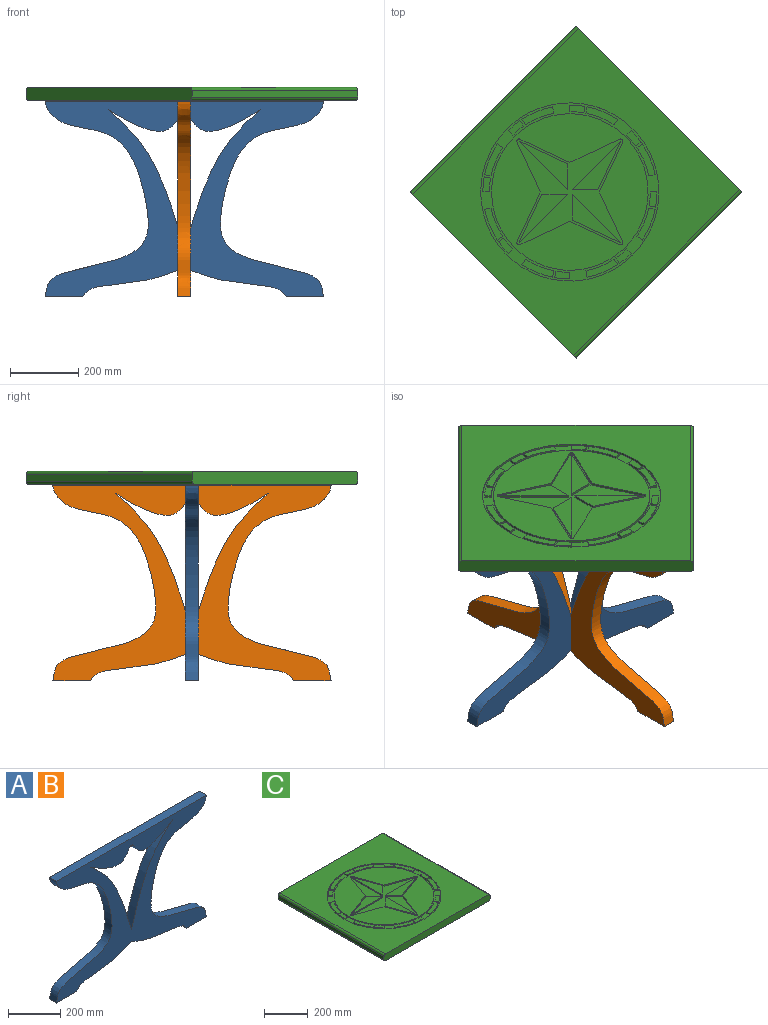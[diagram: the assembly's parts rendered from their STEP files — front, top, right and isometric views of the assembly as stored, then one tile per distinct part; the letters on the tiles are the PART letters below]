
ASSEMBLY  parts=3 mates=1
PART A: 13 faces, bbox 812.8x38.1x571.5 mm
  f0: extruded ~296.91x85.34mm, area 12012.6mm2, adj f1,f10,f11,f12
  f1: plane 109.49x38.1mm, normal (0,0,-1), area 4171.7mm2, adj f0,f2,f11,f12
  f2: extruded ~571.5x300.4mm, area 35398.5mm2, adj f1,f3,f11,f12
  f3: plane 812.8x38.1mm, normal (0,0,1), area 30967.7mm2, adj f2,f4,f11,f12
  f4: extruded ~571.5x300.4mm, area 35398.5mm2, adj f3,f5,f11,f12
  f5: plane 109.49x38.1mm, normal (0,0,-1), area 4171.7mm2, adj f4,f10,f11,f12
  f6: extruded ~58.88x53.54mm, area 3171mm2, adj f7,f9,f11,f12
  f7: extruded ~405.73x222.25mm, area 24861.6mm2, adj f6,f8,f11,f12
  f8: extruded ~405.73x222.25mm, area 24861.6mm2, adj f7,f9,f11,f12
  f9: extruded ~58.88x53.54mm, area 3171mm2, adj f6,f8,f11,f12
  f10: extruded ~296.91x85.34mm, area 12012.6mm2, adj f0,f5,f11,f12
  f11: plane 812.8x571.5mm, normal (0,-1,0), area 168324.2mm2, adj f0,f1,f2,f3,f4,f5,f6,f7
  f12: plane 812.8x571.5mm, normal (0,1,0), area 168324.2mm2, adj f0,f1,f2,f3,f4,f5,f6,f7
PART B: same geometry as A
PART C: 123 faces, bbox 685.8x685.8x38.1 mm
  f0: plane 457.2x457.2mm, normal (0,0,1), area 108640mm2, adj f76,f96,f97,f98,f99,f100,f101,f102
  f1: plane 685.8x666.75mm, normal (0,0,1), area 244313.3mm2, adj f3,f5,f9,f10,f59
  f2: plane 685.8x19.05mm, normal (-1,0,0), area 13064.5mm2, adj f3,f5,f8,f10
  f3: plane 685.8x38.1mm, normal (0,-1,0), area 26051.1mm2, adj f1,f2,f4,f6,f7,f8,f9,f10
  f4: plane 685.8x19.05mm, normal (1,0,0), area 13064.5mm2, adj f3,f5,f7,f9
  f5: plane 685.8x38.1mm, normal (0,1,0), area 26051.1mm2, adj f1,f2,f4,f6,f7,f8,f9,f10
  f6: plane 685.8x666.75mm, normal (0,0,-1), area 457257.1mm2, adj f3,f5,f7,f8
  f7: cylinder r=9.53mm len=685.8mm, axis (0,1,0), area 10260.8mm2, adj f3,f4,f5,f6
  f8: cylinder r=9.53mm len=685.8mm, axis (0,-1,0), area 10260.8mm2, adj f2,f3,f5,f6
  f9: cylinder r=9.53mm len=685.8mm, axis (0,-1,0), area 10260.8mm2, adj f1,f3,f4,f5
  f10: cylinder r=9.53mm len=685.8mm, axis (0,1,0), area 10260.8mm2, adj f1,f2,f3,f5
  f11: cylinder r=254mm len=90.1mm, axis (0,0,1), area 623.1mm2, adj f12,f60,f77,f93
  f12: plane 18.77x6.35mm, normal (0.17,-0.98,0), area 121mm2, adj f11,f13,f77,f93
  f13: cylinder r=234.95mm len=82.47mm, axis (0,0,1), area 570.3mm2, adj f12,f60,f77,f93
  f14: cylinder r=254mm len=33.92mm, axis (0,0,1), area 281.5mm2, adj f15,f61,f77,f92
  f15: plane 15.61x10.93mm, normal (0.57,-0.82,0), area 121mm2, adj f14,f16,f77,f92
  f16: cylinder r=234.95mm len=31.37mm, axis (0,0,1), area 260.4mm2, adj f15,f61,f77,f92
  f17: cylinder r=254mm len=33.92mm, axis (0,0,1), area 281.5mm2, adj f18,f62,f77,f91
  f18: plane 15.61x10.93mm, normal (0.82,0.57,0), area 121mm2, adj f17,f19,f77,f91
  f19: cylinder r=234.95mm len=31.37mm, axis (0,0,1), area 260.4mm2, adj f18,f62,f77,f91
  f20: cylinder r=254mm len=90.1mm, axis (0,0,1), area 623.1mm2, adj f21,f63,f77,f90
  f21: plane 15.61x10.93mm, normal (0.57,0.82,0), area 121mm2, adj f20,f22,f77,f90
  f22: cylinder r=234.95mm len=82.47mm, axis (0,0,1), area 570.3mm2, adj f21,f63,f77,f90
  f23: cylinder r=254mm len=44.11mm, axis (0,0,1), area 281.5mm2, adj f24,f64,f77,f89
  f24: plane 18.76x6.35mm, normal (0.17,0.98,0), area 121mm2, adj f23,f25,f77,f89
  f25: cylinder r=234.95mm len=40.8mm, axis (0,0,1), area 260.4mm2, adj f24,f64,f77,f89
  f26: cylinder r=254mm len=90.1mm, axis (0,0,1), area 623.1mm2, adj f27,f65,f77,f88
  f27: plane 18.77x6.35mm, normal (-0.17,0.98,0), area 121mm2, adj f26,f28,f77,f88
  f28: cylinder r=234.95mm len=82.47mm, axis (0,0,1), area 570.3mm2, adj f27,f65,f77,f88
  f29: cylinder r=254mm len=33.92mm, axis (0,0,1), area 281.5mm2, adj f30,f66,f77,f87
  f30: plane 15.61x10.93mm, normal (-0.57,0.82,0), area 121mm2, adj f29,f31,f77,f87
  f31: cylinder r=234.95mm len=31.37mm, axis (0,0,1), area 260.4mm2, adj f30,f66,f77,f87
  f32: cylinder r=254mm len=90.1mm, axis (0,0,1), area 623.1mm2, adj f33,f67,f77,f86
  f33: plane 15.61x10.93mm, normal (-0.82,0.57,0), area 121mm2, adj f32,f34,f77,f86
  f34: cylinder r=234.95mm len=82.47mm, axis (0,0,1), area 570.3mm2, adj f33,f67,f77,f86
  f35: cylinder r=254mm len=44.11mm, axis (0,0,1), area 281.5mm2, adj f36,f68,f77,f85
  f36: plane 18.76x6.35mm, normal (-0.98,0.17,0), area 121mm2, adj f35,f37,f77,f85
  f37: cylinder r=234.95mm len=40.8mm, axis (0,0,1), area 260.4mm2, adj f36,f68,f77,f85
  f38: cylinder r=254mm len=90.1mm, axis (0,0,1), area 623.1mm2, adj f39,f69,f77,f84
  f39: plane 18.77x6.35mm, normal (-0.98,-0.17,0), area 121mm2, adj f38,f40,f77,f84
  f40: cylinder r=234.95mm len=82.47mm, axis (0,0,1), area 570.3mm2, adj f39,f69,f77,f84
  f41: cylinder r=254mm len=33.92mm, axis (0,0,1), area 281.5mm2, adj f42,f70,f77,f83
  f42: plane 15.61x10.93mm, normal (-0.82,-0.57,0), area 121mm2, adj f41,f43,f77,f83
  f43: cylinder r=234.95mm len=31.37mm, axis (0,0,1), area 260.4mm2, adj f42,f70,f77,f83
  f44: cylinder r=254mm len=90.1mm, axis (0,0,1), area 623.1mm2, adj f45,f71,f77,f82
  f45: plane 15.61x10.93mm, normal (-0.57,-0.82,0), area 121mm2, adj f44,f46,f77,f82
  f46: cylinder r=234.95mm len=82.47mm, axis (0,0,1), area 570.3mm2, adj f45,f71,f77,f82
  f47: cylinder r=254mm len=44.11mm, axis (0,0,1), area 281.5mm2, adj f48,f72,f77,f81
  f48: plane 18.76x6.35mm, normal (-0.17,-0.98,0), area 121mm2, adj f47,f49,f77,f81
  f49: cylinder r=234.95mm len=40.8mm, axis (0,0,1), area 260.4mm2, adj f48,f72,f77,f81
  f50: cylinder r=234.95mm len=82.47mm, axis (0,0,1), area 570.3mm2, adj f51,f73,f77,f80
  f51: plane 18.77x6.35mm, normal (-0.98,0.17,0), area 121mm2, adj f50,f52,f77,f80
  f52: cylinder r=254mm len=90.1mm, axis (0,0,1), area 623.1mm2, adj f51,f73,f77,f80
  f53: plane 18.77x6.35mm, normal (0.98,0.17,0), area 121mm2, adj f54,f74,f77,f79
  f54: cylinder r=234.95mm len=82.47mm, axis (0,0,1), area 570.3mm2, adj f53,f55,f77,f79
  f55: plane 15.61x10.93mm, normal (-0.82,-0.57,0), area 121mm2, adj f54,f74,f77,f79
  f56: cylinder r=234.95mm len=40.8mm, axis (0,0,1), area 260.4mm2, adj f57,f75,f77,f78
  f57: plane 19.05x6.35mm, normal (-1,0,0), area 121mm2, adj f56,f58,f77,f78
  f58: cylinder r=254mm len=44.11mm, axis (0,0,1), area 281.5mm2, adj f57,f75,f77,f78
  f59: cylinder r=260.35mm len=520.7mm, axis (0,0,1), area 10387.5mm2, adj f1,f77
  f60: plane 15.61x10.93mm, normal (-0.57,0.82,0), area 121mm2, adj f11,f13,f77,f93
  f61: plane 13.47x13.47mm, normal (-0.71,0.71,0), area 121mm2, adj f14,f16,f77,f92
  f62: plane 13.47x13.47mm, normal (-0.71,-0.71,0), area 121mm2, adj f17,f19,f77,f91
  f63: plane 18.77x6.35mm, normal (-0.17,-0.98,0), area 121mm2, adj f20,f22,f77,f90
  f64: plane 19.05x6.35mm, normal (0,-1,0), area 121mm2, adj f23,f25,f77,f89
  f65: plane 15.61x10.93mm, normal (0.57,-0.82,0), area 121mm2, adj f26,f28,f77,f88
  f66: plane 13.47x13.47mm, normal (0.71,-0.71,0), area 121mm2, adj f29,f31,f77,f87
  f67: plane 18.77x6.35mm, normal (0.98,-0.17,0), area 121mm2, adj f32,f34,f77,f86
  f68: plane 19.05x6.35mm, normal (1,0,0), area 121mm2, adj f35,f37,f77,f85
  f69: plane 15.61x10.93mm, normal (0.82,0.57,0), area 121mm2, adj f38,f40,f77,f84
  f70: plane 13.47x13.47mm, normal (0.71,0.71,0), area 121mm2, adj f41,f43,f77,f83
  f71: plane 18.77x6.35mm, normal (0.17,0.98,0), area 121mm2, adj f44,f46,f77,f82
  f72: plane 19.05x6.35mm, normal (0,1,0), area 121mm2, adj f47,f49,f77,f81
  f73: plane 15.61x10.93mm, normal (0.82,-0.57,0), area 121mm2, adj f50,f52,f77,f80
  f74: cylinder r=254mm len=90.1mm, axis (0,0,1), area 623.1mm2, adj f53,f55,f77,f79
  f75: plane 18.76x6.35mm, normal (0.98,-0.17,0), area 121mm2, adj f56,f58,f77,f78
  f76: cylinder r=228.6mm len=457.2mm, axis (0,0,1), area 9120.7mm2, adj f0,f77
  f77: plane 520.7x520.7mm, normal (0,0,1), area 27946.7mm2, adj f11,f12,f13,f14,f15,f16,f17,f18
  f78: plane 44.11x22.62mm, normal (0,0,1), area 812.8mm2, adj f56,f57,f58,f75
  f79: plane 93.4x52.93mm, normal (0,0,1), area 1790.1mm2, adj f53,f54,f55,f74
  f80: plane 93.4x52.93mm, normal (0,0,1), area 1790.1mm2, adj f50,f51,f52,f73
  f81: plane 44.11x22.62mm, normal (0,0,1), area 812.8mm2, adj f47,f48,f49,f72
  f82: plane 93.4x52.93mm, normal (0,0,1), area 1790.1mm2, adj f44,f45,f46,f71
  f83: plane 44.84x41.93mm, normal (0,0,1), area 812.8mm2, adj f41,f42,f43,f70
  f84: plane 93.4x52.93mm, normal (0,0,1), area 1790.1mm2, adj f38,f39,f40,f69
  f85: plane 44.11x22.62mm, normal (0,0,1), area 812.8mm2, adj f35,f36,f37,f68
  f86: plane 93.4x52.93mm, normal (0,0,1), area 1790.1mm2, adj f32,f33,f34,f67
  f87: plane 44.84x41.93mm, normal (0,0,1), area 812.8mm2, adj f29,f30,f31,f66
  f88: plane 93.4x52.93mm, normal (0,0,1), area 1790.1mm2, adj f26,f27,f28,f65
  f89: plane 44.11x22.62mm, normal (0,0,1), area 812.8mm2, adj f23,f24,f25,f64
  f90: plane 93.4x52.93mm, normal (0,0,1), area 1790.1mm2, adj f20,f21,f22,f63
  f91: plane 44.84x41.93mm, normal (0,0,1), area 812.8mm2, adj f17,f18,f19,f62
  f92: plane 44.84x41.93mm, normal (0,0,1), area 812.8mm2, adj f14,f15,f16,f61
  f93: plane 93.4x52.93mm, normal (0,0,1), area 1790.1mm2, adj f11,f12,f13,f60
  f94: plane 147.4x53.65mm, normal (-0.34,0.94,0), area 996.1mm2, adj f95,f114,f115,f116
  f95: plane 53.65x53.65mm, normal (0.71,0.71,0), area 481.8mm2, adj f94,f114,f115,f116
  f96: plane 151.2x55.03mm, normal (-0.34,0.94,0), area 1021.8mm2, adj f0,f97,f112,f116
  f97: cylinder r=6.35mm len=11.93mm, axis (0,0,1), area 98.5mm2, adj f0,f96,f98,f116
  f98: plane 151.2x55.03mm, normal (-0.34,-0.94,0), area 1021.8mm2, adj f0,f97,f99,f116
  f99: plane 151.2x55.03mm, normal (-0.94,-0.34,0), area 1021.8mm2, adj f0,f98,f100,f116
  f100: cylinder r=6.35mm len=11.93mm, axis (0,0,1), area 98.5mm2, adj f0,f99,f101,f116
  f101: plane 151.2x55.03mm, normal (0.94,-0.34,0), area 1021.8mm2, adj f0,f100,f102,f116
  f102: plane 151.2x55.03mm, normal (0.34,-0.94,0), area 1021.8mm2, adj f0,f101,f103,f116
  f103: cylinder r=6.35mm len=11.93mm, axis (0,0,1), area 98.5mm2, adj f0,f102,f104,f116
  f104: plane 151.2x55.03mm, normal (0.34,0.94,0), area 1021.8mm2, adj f0,f103,f105,f116
  f105: plane 151.2x55.03mm, normal (0.94,0.34,0), area 1021.8mm2, adj f0,f104,f106,f116
  f106: cylinder r=6.35mm len=11.93mm, axis (0,0,1), area 98.5mm2, adj f0,f105,f112,f116
  f107: plane 147.4x53.65mm, normal (-0.94,-0.34,0), area 996.1mm2, adj f108,f116,f117,f118
  f108: plane 53.65x53.65mm, normal (-0.71,0.71,0), area 481.8mm2, adj f107,f116,f117,f118
  f109: plane 147.4x53.65mm, normal (0.34,-0.94,0), area 996.1mm2, adj f113,f116,f119,f120
  f110: plane 147.4x53.65mm, normal (0.94,0.34,0), area 996.1mm2, adj f111,f116,f121,f122
  f111: plane 53.65x53.65mm, normal (0.71,-0.71,0), area 481.8mm2, adj f110,f116,f121,f122
  f112: plane 151.2x55.03mm, normal (-0.94,0.34,0), area 1021.8mm2, adj f0,f96,f106,f116
  f113: plane 53.65x53.65mm, normal (-0.71,-0.71,0), area 481.8mm2, adj f109,f116,f119,f120
  f114: plane 201.05x53.65mm, normal (0,0,1), area 5393.3mm2, adj f94,f95,f115
  f115: plane 201.05x6.35mm, normal (0,-1,0), area 1276.7mm2, adj f94,f95,f114,f116
  f116: plane 432.77x432.77mm, normal (0,0,1), area 33960.1mm2, adj f94,f95,f96,f97,f98,f99,f100,f101
  f117: plane 201.05x53.65mm, normal (0,0,1), area 5393.3mm2, adj f107,f108,f118
  f118: plane 201.05x6.35mm, normal (1,0,0), area 1276.7mm2, adj f107,f108,f116,f117
  f119: plane 201.05x53.65mm, normal (0,0,1), area 5393.3mm2, adj f109,f113,f120
  f120: plane 201.05x6.35mm, normal (0,1,0), area 1276.7mm2, adj f109,f113,f116,f119
  f121: plane 201.05x53.65mm, normal (0,0,1), area 5393.3mm2, adj f110,f111,f122
  f122: plane 201.05x6.35mm, normal (-1,0,0), area 1276.7mm2, adj f110,f111,f116,f121
PLACE A t=(-258.14,26.75,-50.64)mm
PLACE B rot(axis=(0,0,1),90deg) t=(-277.19,7.7,-50.64)mm
PLACE C rot(axis=(0,0,-1),45deg) t=(-253.83,7.61,523.05)mm
MATE fastened B.f5 <-> A.f1  axis (0,0,-1) through (-258.14,-398.7,-50.64)mm
